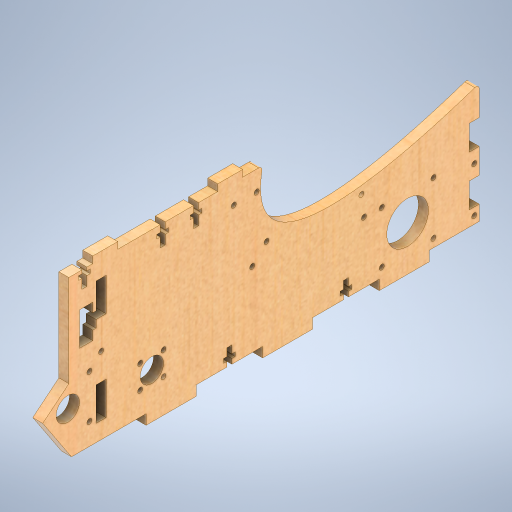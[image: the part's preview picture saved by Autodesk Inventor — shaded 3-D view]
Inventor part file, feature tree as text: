
AUTODESK INVENTOR PART (.ipt)
format: ipt  version: 2024.2 (Build 282272000, 272)  size: 744,448 bytes
history: native  units: mm
features: extrude x14, sketch x14, other x4, fillet x1, reference x1
ambient origin geometry x8: Origin, YZ Plane, XZ Plane, XY Plane, X Axis, Y Axis, Z Axis, Center Point
bodies: Body1 (feature_tree)
feature tree (34):
  other  "Твердое тело1"
  extrude  "Выдавливание1"  Depth=230.0mm
  extrude  "Выдавливание2"  Depth=100.0mm
  extrude  "Выдавливание3"  Depth=6.0mm TaperAngle=0.0deg
  extrude  "Выдавливание4"  Depth=30.0mm
  extrude  "Выдавливание5"  Depth=30.0mm
  extrude  "Выдавливание6"  Depth=40.0mm
  extrude  "Выдавливание7"  Depth=30.0mm
  extrude  "Выдавливание8"  Depth=30.0mm
  extrude  "Выдавливание9"  Depth=40.0mm
  fillet  "Сопряжение1"  [1 undecoded]
  extrude  "Выдавливание11"  Depth=6.0mm
  extrude  "Выдавливание12"  Depth=6.0mm
  extrude  "Выдавливание13"  Depth=10.0mm
  extrude  "Выдавливание14"  Depth=10.0mm
  extrude  "Выдавливание10"  Depth=20.0mm
  sketch  "Эскиз1"
  sketch  "Эскиз2"
  sketch  "Эскиз3"
  sketch  "Эскиз4"
  sketch  "Эскиз5"
  sketch  "Эскиз6"
  sketch  "Эскиз7"
  sketch  "Эскиз8"
  sketch  "Эскиз9"
  sketch  "Эскиз10"
  sketch  "Эскиз11"
  sketch  "Эскиз12"
  reference  "Ссылка1"
  sketch  "Эскиз13"
  sketch  "Эскиз14"
  other  "<userpath>\Documents\Artist-v2\3D\Робот.iam"
  other  "Робот.iam"
  other  "крышка:1"
note: 1 required parameter value undecoded (feature->parameter linkage not recoverable at this tier; creation-order binding heuristic only, values carry confidence <= 0.55)
